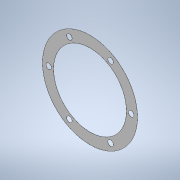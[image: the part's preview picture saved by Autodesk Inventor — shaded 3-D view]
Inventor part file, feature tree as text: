
AUTODESK INVENTOR PART (.ipt)
format: ipt  version: 2020 (Build 240168000, 168)  size: 116,736 bytes
history: native  units: mm
features: other x3, plane x1, extrude x1, sketch x1, reference x1
ambient origin geometry x8: Origin, YZ Plane, XZ Plane, XY Plane, X Axis, Y Axis, Z Axis, Center Point
bodies: 实体1 (feature_tree)
feature tree (7):
  plane  "工作平面1"
  extrude  "拉伸1"  [1 undecoded]
  sketch  "草图1"  dims[d0=0.18mm d1=0.0mm]
  reference  "参考1"
  other  "<userpath>\Desktop\ME_course_project\课设试试\shaft_try_1.iam"
  other  "shaft_try_1.iam"
  other  "轴承端盖2:1"
note: 1 required parameter value undecoded (feature->parameter linkage not recoverable at this tier; creation-order binding heuristic only, values carry confidence <= 0.55)
